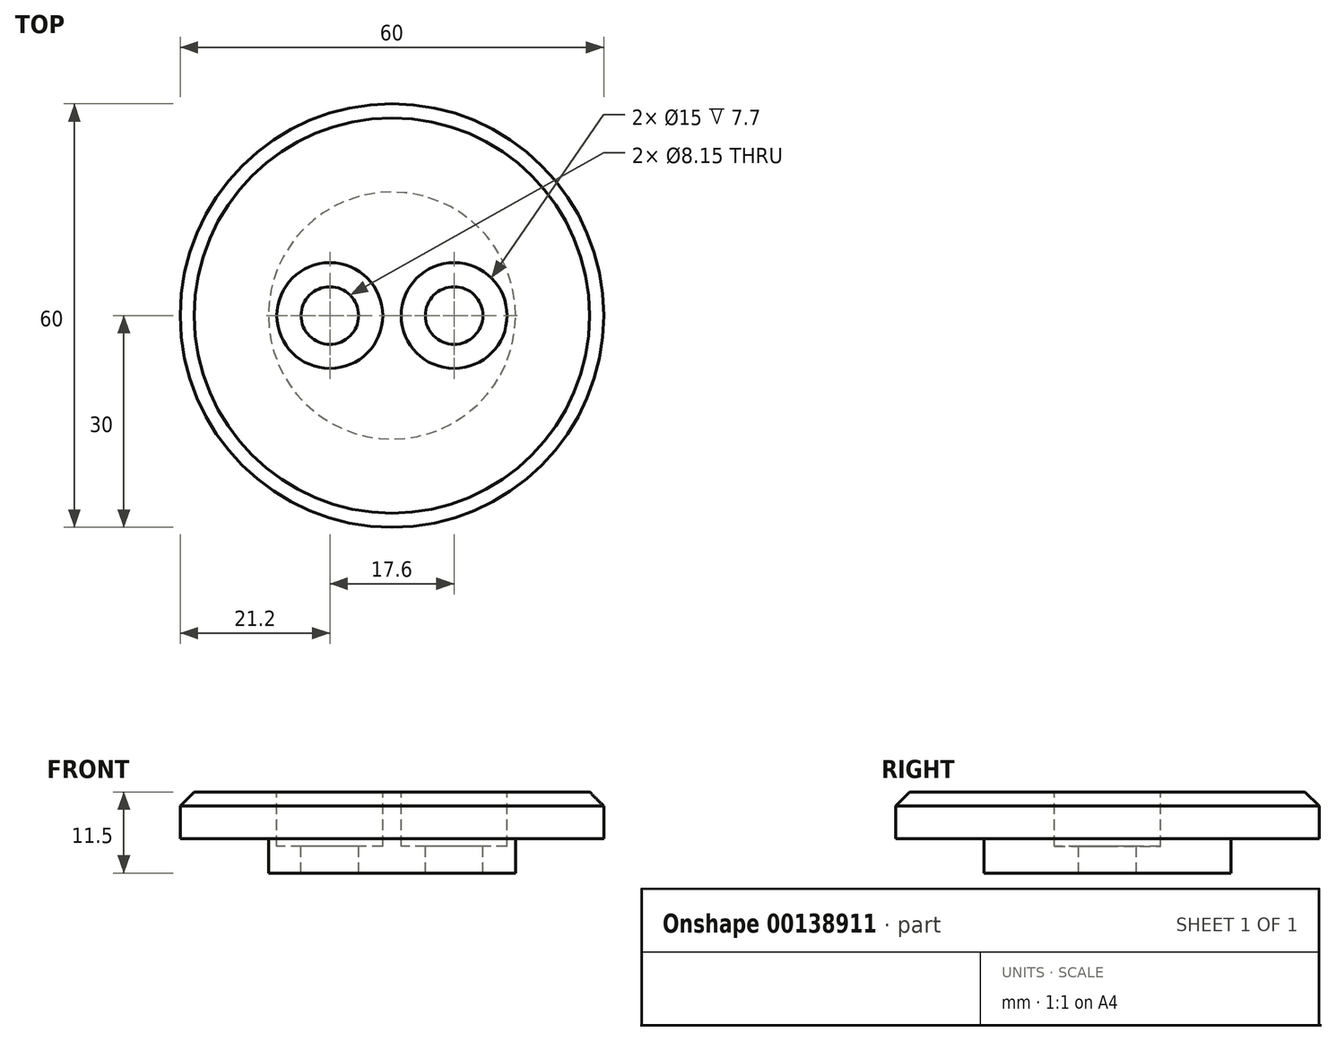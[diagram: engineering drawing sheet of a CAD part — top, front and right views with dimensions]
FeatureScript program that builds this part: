
annotation { "Feature Type Name" : "Feature", "Feature Type Description" : "" }
export const myFeature = defineFeature(function(context is Context, id is Id, definition is map)
    precondition{}
    {
        {
            var Q0;
            Q0=qCreatedBy(makeId("Top.planeOp"),FACE);
            var sketch = newSketch(context, id + "F0", { "sketchPlane" : qUnion([Q0])});
            skCircle(sketch, "E0", {"center": v(0, 0) * mm, "radius": 17.5 * mm});
            skSolve(sketch);
        }
        {
            var Q0;
            Q0 = qSketchRegion(id + "F0", true);
            extrude(context, id + "F1", {"entities" : qUnion([Q0]), "depth" : 4.9 * mm});
        }
        {
            var Q0;
            Q0=makeQuery(id+"F1.opExtrude","CAP_FACE",FACE,{"disambiguationData":[OSD([sQuery(id+"F0.wireOp",EDGE,"E0")])],"isStart":false});
            var sketch = newSketch(context, id + "F2", { "sketchPlane" : qUnion([Q0])});
            skCircle(sketch, "E1", {"center": v(0, 0) * mm, "radius": 30 * mm});
            skSolve(sketch);
        }
        {
            var Q0;
            Q0 = qSketchRegion(id + "F2", true);
            extrude(context, id + "F3", {"entities" : qUnion([Q0]), "operationType" : NewBodyOperationType.ADD, "depth" : 6.6 * mm});
        }
        {
            var Q0;
            Q0=makeQuery(id+"F3.opExtrude","CAP_EDGE",EDGE,{"disambiguationData":[OSD([sQuery(id+"F2.wireOp",EDGE,"E1")])],"isStart":false});
            chamfer(context, id + "F4", {"entities" : qUnion([Q0]), "width" : 2 * mm, "tangentPropagation" : true});
        }
        {
            var Q0;
            Q0=makeQuery(id+"F3.opExtrude","CAP_FACE",FACE,{"disambiguationData":[OSD([sQuery(id+"F2.wireOp",EDGE,"E1")])],"isStart":false});
            var sketch = newSketch(context, id + "F5", { "sketchPlane" : qUnion([Q0])});
            skCircle(sketch, "E2", {"center": v(-8.8, 0) * mm, "radius": 7.5 * mm});
            skCircle(sketch, "E3", {"center": v(-8.8, 0) * mm, "radius": 4.08 * mm});
            skCircle(sketch, "E4.MirrorC", {"center": v(8.8, 0) * mm, "radius": 7.5 * mm});
            skCircle(sketch, "E5.MirrorC", {"center": v(8.8, 0) * mm, "radius": 4.08 * mm});
            skSolve(sketch);
        }
        {
            var Q0;
            Q0 = qSketchRegion(id + "F5", true);
            extrude(context, id + "F6", {"entities" : qUnion([Q0]), "operationType" : NewBodyOperationType.REMOVE, "oppositeDirection" : true, "depth" : 7.7 * mm});
        }
        {
            var Q0;
            Q0=makeQuery(id+"F6.boolean.opBoolean","SPLIT",FACE,{"disambiguationData":[TD([makeQuery(id+"F6.opExtrude","SWEPT_FACE",FACE,{"disambiguationData":[OSD([sQuery(id+"F5.wireOp",EDGE,"E3")])]})])],"derivedFrom":makeQuery(id+"F3.opExtrude","CAP_FACE",FACE,{"disambiguationData":[OSD([sQuery(id+"F2.wireOp",EDGE,"E1")])],"isStart":false})});
            var Q1;
            Q1=makeQuery(id+"F6.boolean.opBoolean","SPLIT",FACE,{"disambiguationData":[TD([makeQuery(id+"F6.opExtrude","SWEPT_FACE",FACE,{"disambiguationData":[OSD([sQuery(id+"F5.wireOp",EDGE,"E5.MirrorC")])]})])],"derivedFrom":makeQuery(id+"F3.opExtrude","CAP_FACE",FACE,{"disambiguationData":[OSD([sQuery(id+"F2.wireOp",EDGE,"E1")])],"isStart":false})});
            extrude(context, id + "F7", {"entities" : qUnion([Q0, Q1]), "operationType" : NewBodyOperationType.REMOVE, "endBound" : BoundingType.THROUGH_ALL, "oppositeDirection" : true, "depth" : 25 * mm});
        }
    });
